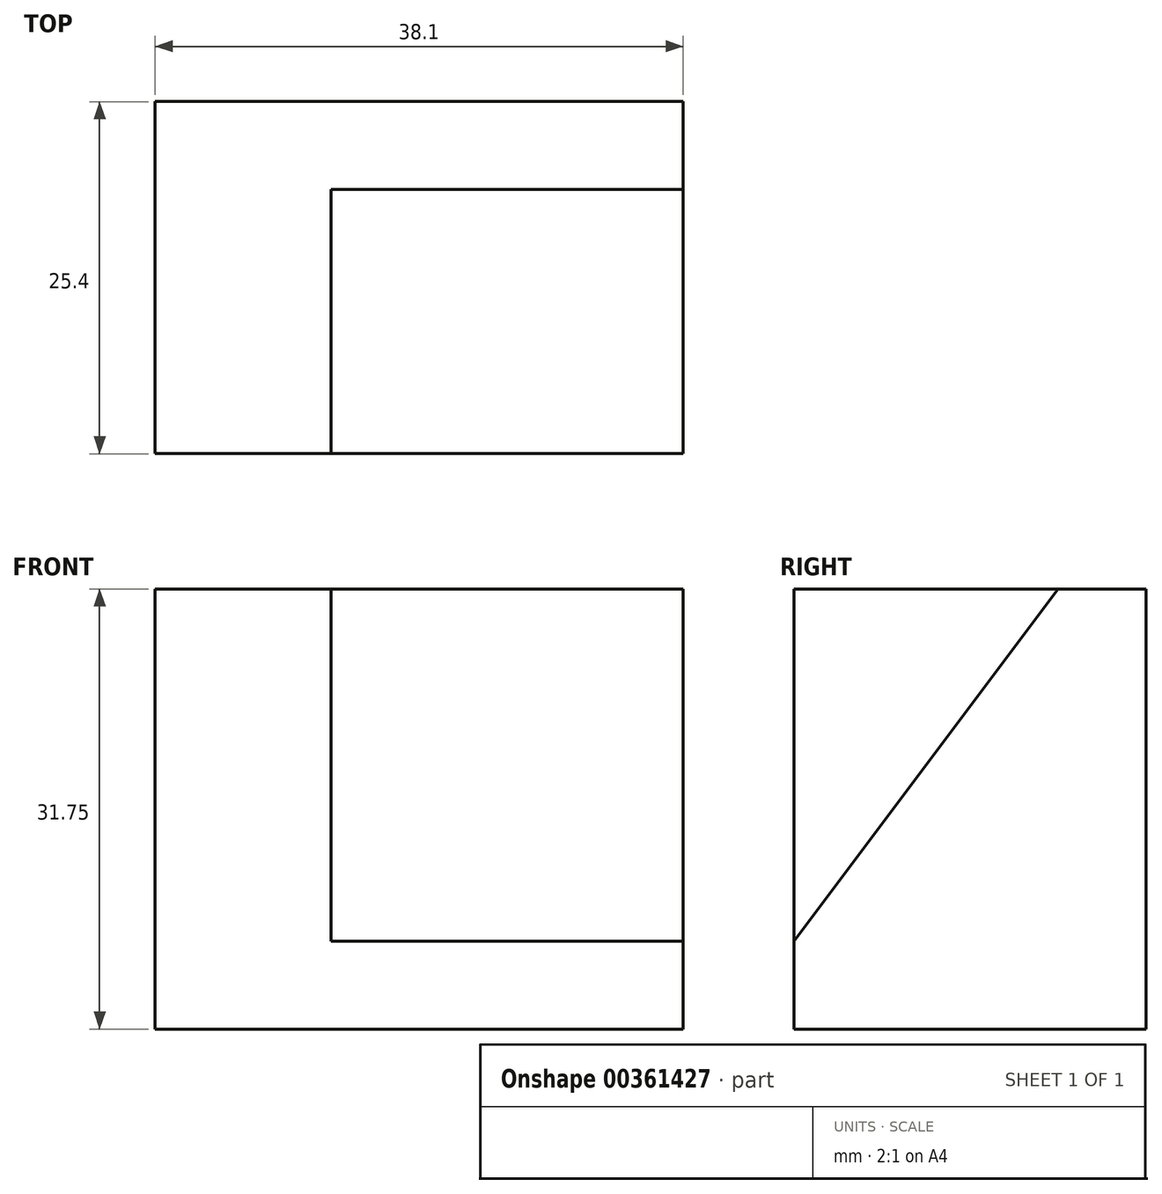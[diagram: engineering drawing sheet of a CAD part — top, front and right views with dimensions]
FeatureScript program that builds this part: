
annotation { "Feature Type Name" : "Feature", "Feature Type Description" : "" }
export const myFeature = defineFeature(function(context is Context, id is Id, definition is map)
    precondition{}
    {
        {
            var Q0;
            Q0=qCreatedBy(makeId("Right.planeOp"),FACE);
            var sketch = newSketch(context, id + "F0", { "sketchPlane" : qUnion([Q0])});
            skLineSegment(sketch, "E0", {"start": v(0, 0) * mm, "end": v(-22.8, 0) * mm});
            skLineSegment(sketch, "E1", {"start": v(-22.8, 0) * mm, "end": v(-22.8, 31.75) * mm});
            skLineSegment(sketch, "E2", {"start": v(-22.8, 31.75) * mm, "end": v(2.6, 31.75) * mm});
            skLineSegment(sketch, "E3", {"start": v(2.6, 31.75) * mm, "end": v(2.6, 0) * mm});
            skLineSegment(sketch, "E4", {"start": v(2.6, 0) * mm, "end": v(-22.8, 0) * mm});
            skSolve(sketch);
        }
        {
            var Q0;
            Q0 = qSketchRegion(id + "F0", true);
            extrude(context, id + "F1", {"entities" : qUnion([Q0]), "depth" : 38.1 * mm});
        }
        {
            var Q0;
            Q0=makeQuery(id+"F1.opExtrude","CAP_FACE",FACE,{"disambiguationData":[OSD([sQuery(id+"F0.wireOp",EDGE,"E1"),sQuery(id+"F0.wireOp",EDGE,"E2"),sQuery(id+"F0.wireOp",EDGE,"E3"),sQuery(id+"F0.wireOp",EDGE,"E4")])],"isStart":false});
            var sketch = newSketch(context, id + "F2", { "sketchPlane" : qUnion([Q0])});
            skLineSegment(sketch, "E5", {"start": v(-22.8, 31.75) * mm, "end": v(-3.76, 31.75) * mm});
            skLineSegment(sketch, "E6", {"start": v(-3.76, 31.75) * mm, "end": v(-22.8, 6.35) * mm});
            skLineSegment(sketch, "E7", {"start": v(-22.8, 6.35) * mm, "end": v(-22.8, 31.75) * mm});
            skSolve(sketch);
        }
        {
            var Q0;
            Q0 = qSketchRegion(id + "F2", true);
            extrude(context, id + "F3", {"entities" : qUnion([Q0]), "operationType" : NewBodyOperationType.REMOVE, "oppositeDirection" : true, "depth" : 25.4 * mm});
        }
    });
